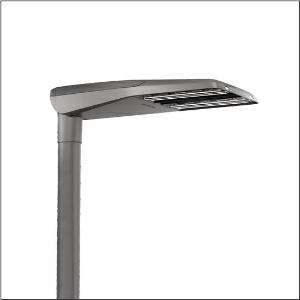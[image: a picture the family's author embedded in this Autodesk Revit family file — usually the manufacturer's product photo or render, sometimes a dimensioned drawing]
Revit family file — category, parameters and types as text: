
# Revit family: streetlight_sl_11_iq_midi___pc-r_5xc3f11g08me_10ab
name_source: partatom
category: Lighting Fixtures
units: mm (PartAtom-declared; Revit-internal decimal feet)

## family parameters
Cut with Voids When Loaded = No
Host = Face
Light Source = No
Part Type = Normal
Room Calculation Point = No
Round Connector Dimension = Use Diameter
Shared = No

## types (1)
- --- (1 x LED, 9590 lm, 124.5 W, 1800K)
    Apparent Load = 125 VA
    CIE Flux Codes = 37 73 96 100 100
    Color Rendering = 70
    Color Temperature = 1800K
    Default Elevation = 1800 mm  [stored 5.90551 ft]
    Description = Streetlight SL 11 iQ midi, mast luminaire, primary light control with 3 zone facetted reflector, of plastic, silver coated, highly specular, primary optical cover: cover, of PMMA, transparent, light distribution: PC-R, light emission: direct distribution, primary light characteristic: asymmetric, right, installation type: post-top, side-entry, LED, High Power LED, rated luminous flux: 9.590lm, luminous efficacy: 77lm/W, light colour: 718, colour temperature: 1800K, control: Street-Remote, Auto-Match, Temp-Guard, Lumen-Switch, Night-Set, Smart-Wire, Light-Fading, Desk-Remote (wireless, voltage-free reading and setting of iQ features in the workshop via application-optimized NFC function/RFID function), optimised constant luminous flux control (CLO 2.0), presetting dimming linear, with cable H07RN-F 5x 1.5mm², mains connection: 230..240V, AC, 50/60Hz, connection cable pre-assembled, cable length: 12,5m, start of lifetime: 125W, end of service life: 132W, reduction: 55W, luminaire housing, of diecast aluminium, powder-coated, Siteco® metallic grey (DB 702S), please order mast flange separately, inclination adjustable without tools: 0°, 5°, 10°, 15° (post-top) | 0°, -5°, -10°, -15° (side-entry), sealing non-destructively replaceable, multi-level sealing system, length: 780mm, width: 376mm, height: 118mm, mast flange for spigot size: 42mm (side-entry): 5XC10008XM4, 60/48mm (side-entry/post-top): 5XC10108XM2, 76/60mm (side-entry/post-top): 5XC10108XM1, equipment: Power, protection rating (complete): IP66, insulation class (complete): insulation class II (safety insulation), certification: CE, ENEC, VDE, impact resistance: IK09, permissible operating ambient temperature for outdoor applications: -25..+50°C, standard-compliant lighting for roads and squares, Environmental Product Declaration (EPD) tested and certified by an independent institute, packaging unit: 1 piece

Light Distribution: PC-R
    Height = 118 mm
    Lamp = 1 x LED
    Lamp Light Flux = 9590 lm
    Lamp Power = 124.5 W
    Lamp count = 1
    Length = 780 mm
    Luminous efficacy = 77 lm/W
    Manufacturer = Siteco
    ModVariant = No
    Model = 5XC3F11G08ME
    Number of Poles = 1
    OnlyDefault = Yes
    Power Factor = 1
    Product Name = Streetlight SL 11 iQ midi | PC-R
    Product group = mast luminaire | pylon top
    ProductGroupID = 6100
    Protection Class = Protection class II
    Protection Degree = IP 66
    RLX_Detail_Level = 1
    RLX_Emergency_Light_Flux = 0 lm
    RLX_Emergency_Type = 0
    RLX_Emergency_Type_DB = No
    RlxData = <blob elided: 74473 chars, md5=f819ad72>
    Socket = socket
    Standby Power = 0 W
    System Light Flux = 9590 lm
    System Power = 125 W
    Type Comments = factory setting: luminous flux: 100 % | dim-lin: 254 | 554 mA
    Type Image = l_1005960.jpg
    URL = http://relux.com
    VarID = @adj_028759
    Voltage = 0 V
    Weight = 0.00 kg
    Width = 376 mm

note: [stored X ft] marks values corroborated as IEEE doubles in the binary element streams (Revit-internal decimal feet)

## geometry (parser evidence)
native form markers: Blend x4, Sweep x11
no freeform markers — native parametric forms only
